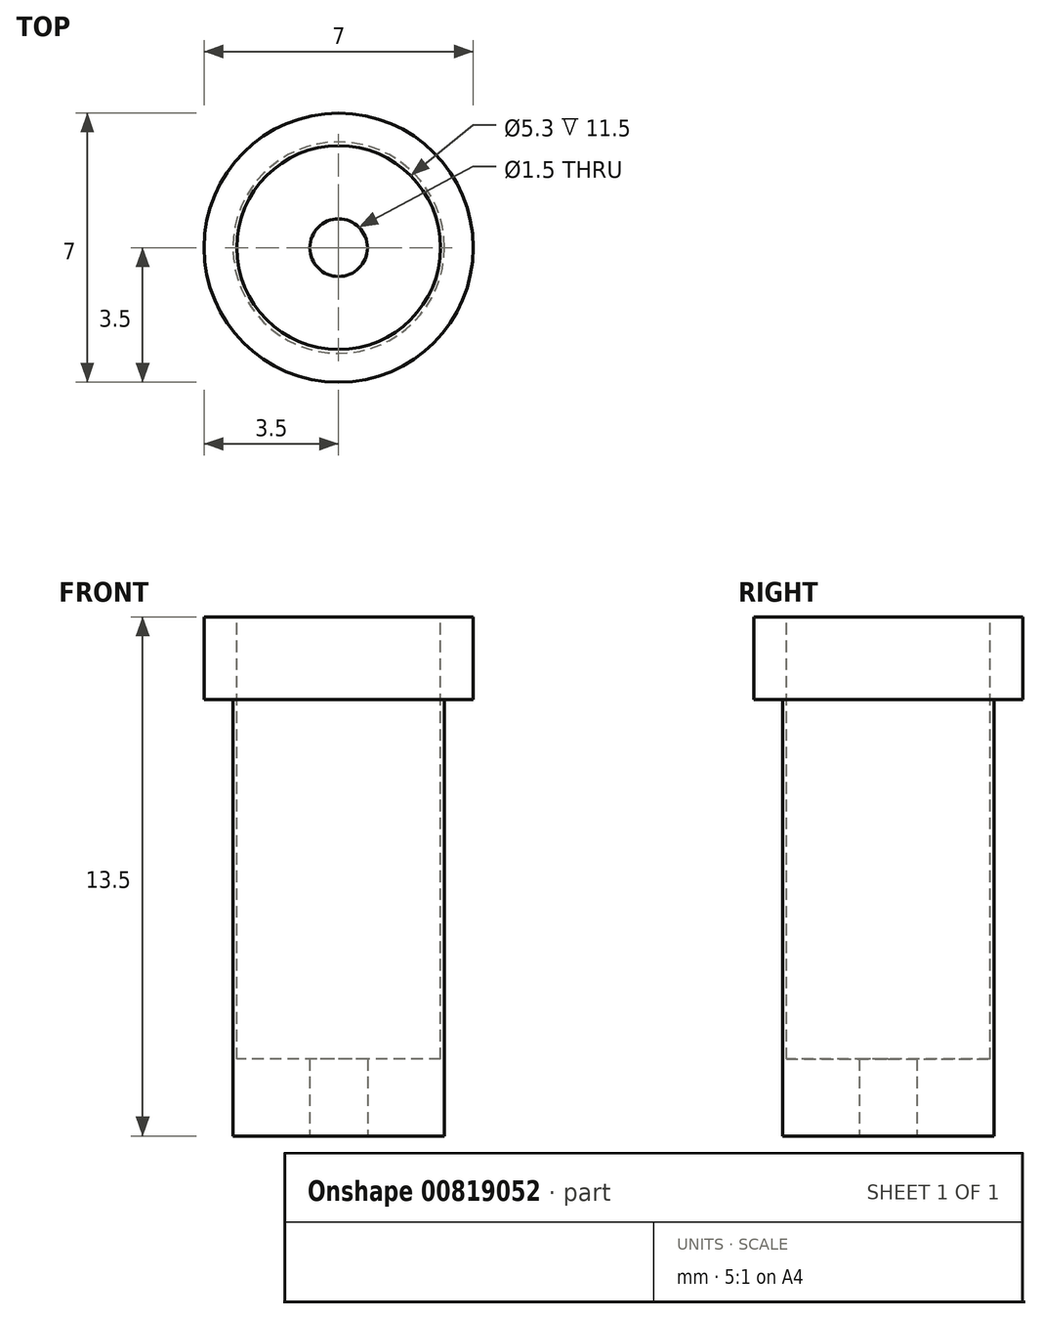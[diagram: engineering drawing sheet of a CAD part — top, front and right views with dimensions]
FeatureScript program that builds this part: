
annotation { "Feature Type Name" : "Feature", "Feature Type Description" : "" }
export const myFeature = defineFeature(function(context is Context, id is Id, definition is map)
    precondition{}
    {
        {
            var Q0;
            Q0=qCreatedBy(makeId("Top.planeOp"),FACE);
            var sketch = newSketch(context, id + "F0", { "sketchPlane" : qUnion([Q0])});
            skCircle(sketch, "E0", {"center": v(0, 0) * mm, "radius": 3.5 * mm});
            skSolve(sketch);
        }
        {
            var Q0;
            Q0 = qSketchRegion(id + "F0", true);
            var Q1;
            Q1=makeQuery(id+"F0.imprint","IMPRINT",FACE,{"disambiguationData":[TD([[makeQuery(id+"F0.imprint","IMPRINT",EDGE,{"derivedFrom":sQuery(id+"F0.wireOp",EDGE,"E0")}),1.0]])]});
            extrude(context, id + "F1", {"entities" : qUnion([Q0, Q1]), "depth" : 2.15 * mm, "offsetDistance" : 25 * mm});
        }
        {
            var Q0;
            Q0=qCreatedBy(makeId("Top.planeOp"),FACE);
            var sketch = newSketch(context, id + "F2", { "sketchPlane" : qUnion([Q0])});
            skCircle(sketch, "E1", {"center": v(0, 0) * mm, "radius": 2.75 * mm});
            skSolve(sketch);
        }
        {
            var Q0;
            Q0 = qSketchRegion(id + "F2", true);
            extrude(context, id + "F3", {"entities" : qUnion([Q0]), "operationType" : NewBodyOperationType.ADD, "oppositeDirection" : true, "depth" : 11.35 * mm, "offsetDistance" : 25 * mm});
        }
        {
            var Q0;
            Q0=makeQuery(id+"F1.opExtrude","CAP_FACE",FACE,{"disambiguationData":[OSD([sQuery(id+"F0.wireOp",EDGE,"E0")])],"isStart":false});
            var sketch = newSketch(context, id + "F4", { "sketchPlane" : qUnion([Q0])});
            skCircle(sketch, "E2", {"center": v(0, 0) * mm, "radius": 2.65 * mm});
            skSolve(sketch);
        }
        {
            var Q0;
            Q0 = qSketchRegion(id + "F4", true);
            extrude(context, id + "F5", {"entities" : qUnion([Q0]), "operationType" : NewBodyOperationType.REMOVE, "oppositeDirection" : true, "depth" : 11.5 * mm, "offsetDistance" : 25 * mm});
        }
        {
            var Q0;
            Q0=makeQuery(id+"F3.opExtrude","CAP_FACE",FACE,{"disambiguationData":[OSD([sQuery(id+"F2.wireOp",EDGE,"E1")])],"isStart":false});
            var sketch = newSketch(context, id + "F6", { "sketchPlane" : qUnion([Q0])});
            skCircle(sketch, "E3", {"center": v(0, 0) * mm, "radius": 0.75 * mm});
            skSolve(sketch);
        }
        {
            var Q0;
            Q0 = qSketchRegion(id + "F6", true);
            extrude(context, id + "F7", {"entities" : qUnion([Q0]), "operationType" : NewBodyOperationType.REMOVE, "endBound" : BoundingType.THROUGH_ALL, "oppositeDirection" : true, "depth" : 25 * mm, "offsetDistance" : 25 * mm});
        }
    });
